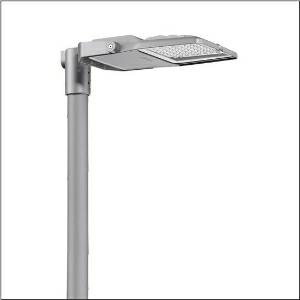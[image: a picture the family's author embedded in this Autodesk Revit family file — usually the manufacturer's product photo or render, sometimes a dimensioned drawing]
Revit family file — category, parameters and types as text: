
# Revit family: floodlight_fl_21_mini___pl61_5xa7776c4c3a_c7e0
name_source: partatom
category: Lighting Fixtures
units: mm (PartAtom-declared; Revit-internal decimal feet)

## family parameters
Cut with Voids When Loaded = No
Host = Face
Light Source = No
Part Type = Normal
Room Calculation Point = No
Round Connector Dimension = Use Diameter
Shared = No

## types (1)
- --- (1 x LED, 12460 lm, 89 W, 4000K)
    Apparent Load = 89 VA
    CIE Flux Codes = 33 65 98 100 100
    Color Rendering = 70
    Color Temperature = 4000K
    Default Elevation = 1800 mm
    Description = Floodlight FL 21 mini, floodlight, primary light control with lens, of PMMA, primary optical cover: protective disc, of toughened safety glass, transparent, light distribution: PL61, light emission: direct distribution, installation type: surface-mounted, LED, High Power LED, rated luminous flux: 12.460lm, luminous efficacy: 140lm/W, light colour: 740, colour temperature: 4000K, control gear: D4iSmart Interface (Zhaga), control: overheat protection, constant luminous flux control, time-dependent luminous flux control, flexible luminous flux parameterisation, pre-setting: logarithmic dimming characteristic, with terminal, 6-pole, mains connection: 220..240V, AC, 50/60Hz, start of lifetime: 89W, end of service life: 94W, reduction: 43W, mast bracket, of diecast aluminium, powder-coated, SITECO metallic grey (DB 702S), corrosivity category C5 mid according to DIN EN ISO 12944, suitable for swimming pools, chlorine-resistant, sealing non-destructively replaceable, mast bracket, of steel, galvanised, powder-coated, SITECO metallic grey (DB 702S), Smart Interface below and above, protection rating (complete): IP66, insulation class (complete): insulation class II (safety insulation), certification: CE, ENEC, VDE, protection symbol: D, impact resistance: IK08, permissible operating ambient temperature: -40..+40°C, permissible operating ambient temperature for outdoor applications: -40..+50°C, standard: DIN EN 12944, LABS conformity tested according to VDMA 24364:2018-05, packaging unit: 1 piece

Light Distribution: PL61
    Height = 70 mm
    Lamp = 1 x LED
    Lamp Light Flux = 12460 lm
    Lamp Power = 89 W
    Lamp count = 1
    Length = 485 mm
    Luminous efficacy = 140 lm/W
    Manufacturer = Siteco
    ModVariant = No
    Model = 5XA7776C4C3A
    Number of Poles = 1
    OnlyDefault = Yes
    Power Factor = 1
    Product Name = Floodlight FL 21 mini | PL61
    Product group = floodlight | pylon annexe
    ProductGroupID = 6201
    Protection Class = Protection class II
    Protection Degree = IP 66
    RLX_Detail_Level = 1
    RLX_Emergency_Light_Flux = 0 lm
    RLX_Emergency_Type = 0
    RLX_Emergency_Type_DB = No
    RlxData = <blob elided: 101089 chars, md5=68872f6c>
    Socket = socket
    Standby Power = 0 W
    System Light Flux = 12460 lm
    System Power = 89 W
    Type Comments = factory setting: luminous flux: 100 % | dim-lin: 254 | 456 mA
    Type Image = l_1007125.jpg
    URL = http://relux.com
    VarID = @adj_102087
    Voltage = 0 V
    Weight = 0.00 kg
    Width = 337 mm

## geometry (parser evidence)
native form markers: Blend x4, Sweep x14
no freeform markers — native parametric forms only
